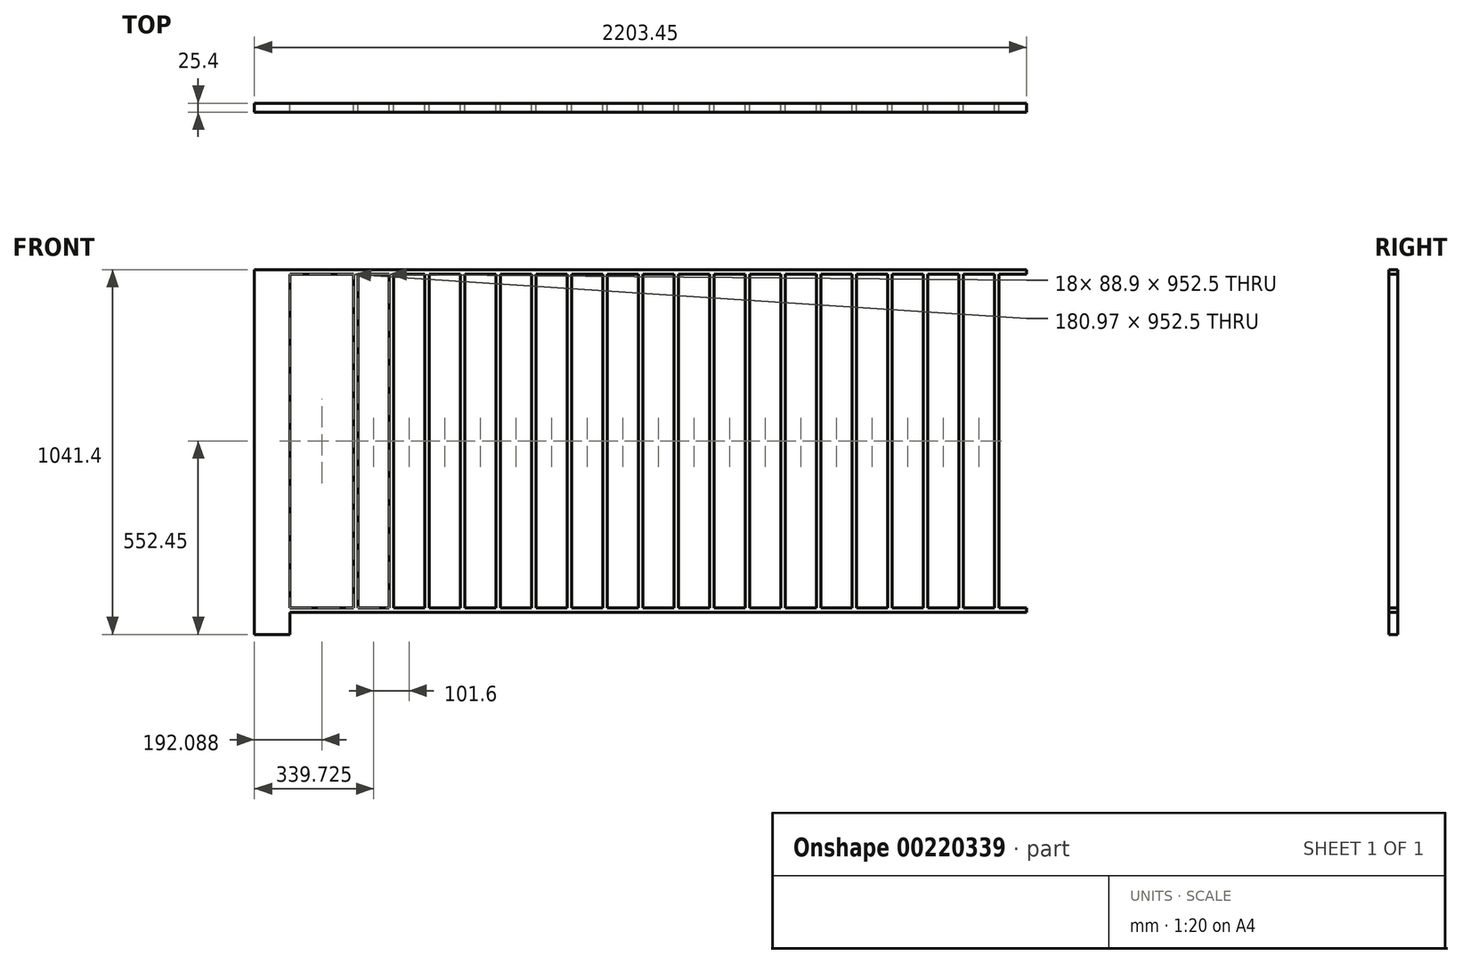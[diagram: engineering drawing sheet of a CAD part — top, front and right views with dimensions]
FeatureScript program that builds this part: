
annotation { "Feature Type Name" : "Feature", "Feature Type Description" : "" }
export const myFeature = defineFeature(function(context is Context, id is Id, definition is map)
    precondition{}
    {
        {
            var Q0;
            Q0=qCreatedBy(makeId("Front.planeOp"),FACE);
            var sketch = newSketch(context, id + "F0", { "sketchPlane" : qUnion([Q0])});
            skLineSegment(sketch, "E0.bottom", {"start": v(0, 0) * mm, "end": v(101.6, 0) * mm});
            skLineSegment(sketch, "E0.top", {"start": v(0, 1041.4) * mm, "end": v(101.6, 1041.4) * mm});
            skLineSegment(sketch, "E0.left", {"start": v(0, 0) * mm, "end": v(0, 1041.4) * mm});
            skLineSegment(sketch, "E0.right", {"start": v(101.6, 0) * mm, "end": v(101.6, 1041.4) * mm});
            skLineSegment(sketch, "E1.bottom", {"start": v(101.6, 63.5) * mm, "end": v(2203.45, 63.5) * mm});
            skLineSegment(sketch, "E1.top", {"start": v(101.6, 76.2) * mm, "end": v(2203.45, 76.2) * mm});
            skLineSegment(sketch, "E1.left", {"start": v(101.6, 63.5) * mm, "end": v(101.6, 76.2) * mm});
            skLineSegment(sketch, "E1.right", {"start": v(2203.45, 63.5) * mm, "end": v(2203.45, 76.2) * mm});
            skLineSegment(sketch, "E2.bottom", {"start": v(101.6, 1028.7) * mm, "end": v(2203.45, 1028.7) * mm});
            skLineSegment(sketch, "E2.top", {"start": v(101.6, 1041.4) * mm, "end": v(2203.45, 1041.4) * mm});
            skLineSegment(sketch, "E2.left", {"start": v(101.6, 1028.7) * mm, "end": v(101.6, 1041.4) * mm});
            skLineSegment(sketch, "E2.right", {"start": v(2203.45, 1028.7) * mm, "end": v(2203.45, 1041.4) * mm});
            skLineSegment(sketch, "E3.bottom", {"start": v(180.98, 76.2) * mm, "end": v(193.68, 76.2) * mm});
            skLineSegment(sketch, "E3.top", {"start": v(180.97, 1028.7) * mm, "end": v(193.67, 1028.7) * mm});
            skLineSegment(sketch, "E3.left", {"start": v(180.98, 76.2) * mm, "end": v(180.97, 1028.7) * mm});
            skLineSegment(sketch, "E3.right", {"start": v(193.68, 76.2) * mm, "end": v(193.67, 1028.7) * mm});
            skLineSegment(sketch, "E4.1.0.0", {"start": v(282.58, 76.2) * mm, "end": v(282.57, 1028.7) * mm});
            skLineSegment(sketch, "E4.1.0.1", {"start": v(295.28, 76.2) * mm, "end": v(295.27, 1028.7) * mm});
            skLineSegment(sketch, "E4.2.0.0", {"start": v(384.18, 76.2) * mm, "end": v(384.18, 1028.7) * mm});
            skLineSegment(sketch, "E4.2.0.1", {"start": v(396.88, 76.2) * mm, "end": v(396.88, 1028.7) * mm});
            skLineSegment(sketch, "E4.3.0.0", {"start": v(485.78, 76.2) * mm, "end": v(485.78, 1028.7) * mm});
            skLineSegment(sketch, "E4.3.0.1", {"start": v(498.48, 76.2) * mm, "end": v(498.48, 1028.7) * mm});
            skLineSegment(sketch, "E4.4.0.0", {"start": v(587.38, 76.2) * mm, "end": v(587.38, 1028.7) * mm});
            skLineSegment(sketch, "E4.4.0.1", {"start": v(600.08, 76.2) * mm, "end": v(600.08, 1028.7) * mm});
            skLineSegment(sketch, "E4.5.0.0", {"start": v(688.98, 76.2) * mm, "end": v(688.98, 1028.7) * mm});
            skLineSegment(sketch, "E4.5.0.1", {"start": v(701.68, 76.2) * mm, "end": v(701.68, 1028.7) * mm});
            skLineSegment(sketch, "E4.6.0.0", {"start": v(790.58, 76.2) * mm, "end": v(790.58, 1028.7) * mm});
            skLineSegment(sketch, "E4.6.0.1", {"start": v(803.28, 76.2) * mm, "end": v(803.28, 1028.7) * mm});
            skLineSegment(sketch, "E4.7.0.0", {"start": v(892.18, 76.2) * mm, "end": v(892.18, 1028.7) * mm});
            skLineSegment(sketch, "E4.7.0.1", {"start": v(904.88, 76.2) * mm, "end": v(904.88, 1028.7) * mm});
            skLineSegment(sketch, "E4.8.0.0", {"start": v(993.78, 76.2) * mm, "end": v(993.78, 1028.7) * mm});
            skLineSegment(sketch, "E4.8.0.1", {"start": v(1006.48, 76.2) * mm, "end": v(1006.48, 1028.7) * mm});
            skLineSegment(sketch, "E4.9.0.0", {"start": v(1095.38, 76.2) * mm, "end": v(1095.38, 1028.7) * mm});
            skLineSegment(sketch, "E4.9.0.1", {"start": v(1108.08, 76.2) * mm, "end": v(1108.08, 1028.7) * mm});
            skLineSegment(sketch, "E4.10.0.0", {"start": v(1196.98, 76.2) * mm, "end": v(1196.98, 1028.7) * mm});
            skLineSegment(sketch, "E4.10.0.1", {"start": v(1209.68, 76.2) * mm, "end": v(1209.68, 1028.7) * mm});
            skLineSegment(sketch, "E4.11.0.0", {"start": v(1298.58, 76.2) * mm, "end": v(1298.58, 1028.7) * mm});
            skLineSegment(sketch, "E4.11.0.1", {"start": v(1311.28, 76.2) * mm, "end": v(1311.28, 1028.7) * mm});
            skLineSegment(sketch, "E4.12.0.0", {"start": v(1400.18, 76.2) * mm, "end": v(1400.18, 1028.7) * mm});
            skLineSegment(sketch, "E4.12.0.1", {"start": v(1412.88, 76.2) * mm, "end": v(1412.88, 1028.7) * mm});
            skLineSegment(sketch, "E4.13.0.0", {"start": v(1501.78, 76.2) * mm, "end": v(1501.78, 1028.7) * mm});
            skLineSegment(sketch, "E4.13.0.1", {"start": v(1514.48, 76.2) * mm, "end": v(1514.48, 1028.7) * mm});
            skLineSegment(sketch, "E4.14.0.0", {"start": v(1603.38, 76.2) * mm, "end": v(1603.38, 1028.7) * mm});
            skLineSegment(sketch, "E4.14.0.1", {"start": v(1616.08, 76.2) * mm, "end": v(1616.08, 1028.7) * mm});
            skLineSegment(sketch, "E4.15.0.0", {"start": v(1704.98, 76.2) * mm, "end": v(1704.98, 1028.7) * mm});
            skLineSegment(sketch, "E4.15.0.1", {"start": v(1717.68, 76.2) * mm, "end": v(1717.68, 1028.7) * mm});
            skLineSegment(sketch, "E4.16.0.0", {"start": v(1806.58, 76.2) * mm, "end": v(1806.58, 1028.7) * mm});
            skLineSegment(sketch, "E4.16.0.1", {"start": v(1819.28, 76.2) * mm, "end": v(1819.28, 1028.7) * mm});
            skLineSegment(sketch, "E4.17.0.0", {"start": v(1908.18, 76.2) * mm, "end": v(1908.18, 1028.7) * mm});
            skLineSegment(sketch, "E4.17.0.1", {"start": v(1920.88, 76.2) * mm, "end": v(1920.88, 1028.7) * mm});
            skLineSegment(sketch, "E4.direction1", {"start": v(180.98, 76.2) * mm, "end": v(282.58, 76.2) * mm, "construction": true});
            skLineSegment(sketch, "E5.1.0.0", {"start": v(2009.78, 76.2) * mm, "end": v(2009.78, 1028.7) * mm});
            skLineSegment(sketch, "E5.1.0.1", {"start": v(2022.48, 76.2) * mm, "end": v(2022.48, 1028.7) * mm});
            skLineSegment(sketch, "E5.2.0.0", {"start": v(2111.38, 76.2) * mm, "end": v(2111.38, 1028.7) * mm});
            skLineSegment(sketch, "E5.2.0.1", {"start": v(2124.08, 76.2) * mm, "end": v(2124.08, 1028.7) * mm});
            skLineSegment(sketch, "E5.direction1", {"start": v(1908.18, 76.2) * mm, "end": v(2009.78, 76.2) * mm, "construction": true});
            skSolve(sketch);
        }
        {
            var Q0;
            {var subQ1=sQuery(id+"F0.wireOp",EDGE,"E0.bottom");Q0=makeQuery(id+"F0.imprint","IMPRINT",FACE,{"disambiguationData":[TD([[makeQuery(id+"F0.imprint","IMPRINT",EDGE,{"derivedFrom":subQ1}),1.0]])]});}
            var Q1;
            {var subQ24=sQuery(id+"F0.wireOp",EDGE,"E1.bottom");Q1=makeQuery(id+"F0.imprint","IMPRINT",FACE,{"disambiguationData":[TD([[makeQuery(id+"F0.imprint","IMPRINT",EDGE,{"derivedFrom":subQ24}),1.0]])]});}
            var Q2;
            Q2=makeQuery(id+"F0.imprint","IMPRINT",FACE,{"disambiguationData":[TD([[makeQuery(id+"F0.imprint","IMPRINT",EDGE,{"derivedFrom":sQuery(id+"F0.wireOp",EDGE,"E3.bottom")}),1.0]])]});
            var Q3;
            {var subQ0=sQuery(id+"F0.wireOp",EDGE,"E4.1.0.0");Q3=makeQuery(id+"F0.imprint","IMPRINT",FACE,{"disambiguationData":[TD([[makeQuery(id+"F0.imprint","IMPRINT",EDGE,{"derivedFrom":subQ0}),-1.0]])]});}
            var Q4;
            {var subQ0=sQuery(id+"F0.wireOp",EDGE,"E4.2.0.0");Q4=makeQuery(id+"F0.imprint","IMPRINT",FACE,{"disambiguationData":[TD([[makeQuery(id+"F0.imprint","IMPRINT",EDGE,{"derivedFrom":subQ0}),-1.0]])]});}
            var Q5;
            {var subQ0=sQuery(id+"F0.wireOp",EDGE,"E4.3.0.0");Q5=makeQuery(id+"F0.imprint","IMPRINT",FACE,{"disambiguationData":[TD([[makeQuery(id+"F0.imprint","IMPRINT",EDGE,{"derivedFrom":subQ0}),-1.0]])]});}
            var Q6;
            {var subQ0=sQuery(id+"F0.wireOp",EDGE,"E4.4.0.0");Q6=makeQuery(id+"F0.imprint","IMPRINT",FACE,{"disambiguationData":[TD([[makeQuery(id+"F0.imprint","IMPRINT",EDGE,{"derivedFrom":subQ0}),-1.0]])]});}
            var Q7;
            {var subQ0=sQuery(id+"F0.wireOp",EDGE,"E4.5.0.0");Q7=makeQuery(id+"F0.imprint","IMPRINT",FACE,{"disambiguationData":[TD([[makeQuery(id+"F0.imprint","IMPRINT",EDGE,{"derivedFrom":subQ0}),-1.0]])]});}
            var Q8;
            {var subQ0=sQuery(id+"F0.wireOp",EDGE,"E4.6.0.0");Q8=makeQuery(id+"F0.imprint","IMPRINT",FACE,{"disambiguationData":[TD([[makeQuery(id+"F0.imprint","IMPRINT",EDGE,{"derivedFrom":subQ0}),-1.0]])]});}
            var Q9;
            {var subQ0=sQuery(id+"F0.wireOp",EDGE,"E4.7.0.0");Q9=makeQuery(id+"F0.imprint","IMPRINT",FACE,{"disambiguationData":[TD([[makeQuery(id+"F0.imprint","IMPRINT",EDGE,{"derivedFrom":subQ0}),-1.0]])]});}
            var Q10;
            {var subQ0=sQuery(id+"F0.wireOp",EDGE,"E4.8.0.0");Q10=makeQuery(id+"F0.imprint","IMPRINT",FACE,{"disambiguationData":[TD([[makeQuery(id+"F0.imprint","IMPRINT",EDGE,{"derivedFrom":subQ0}),-1.0]])]});}
            var Q11;
            {var subQ0=sQuery(id+"F0.wireOp",EDGE,"E4.9.0.0");Q11=makeQuery(id+"F0.imprint","IMPRINT",FACE,{"disambiguationData":[TD([[makeQuery(id+"F0.imprint","IMPRINT",EDGE,{"derivedFrom":subQ0}),-1.0]])]});}
            var Q12;
            {var subQ0=sQuery(id+"F0.wireOp",EDGE,"E4.10.0.0");Q12=makeQuery(id+"F0.imprint","IMPRINT",FACE,{"disambiguationData":[TD([[makeQuery(id+"F0.imprint","IMPRINT",EDGE,{"derivedFrom":subQ0}),-1.0]])]});}
            var Q13;
            {var subQ0=sQuery(id+"F0.wireOp",EDGE,"E4.11.0.0");Q13=makeQuery(id+"F0.imprint","IMPRINT",FACE,{"disambiguationData":[TD([[makeQuery(id+"F0.imprint","IMPRINT",EDGE,{"derivedFrom":subQ0}),-1.0]])]});}
            var Q14;
            {var subQ0=sQuery(id+"F0.wireOp",EDGE,"E4.12.0.0");Q14=makeQuery(id+"F0.imprint","IMPRINT",FACE,{"disambiguationData":[TD([[makeQuery(id+"F0.imprint","IMPRINT",EDGE,{"derivedFrom":subQ0}),-1.0]])]});}
            var Q15;
            {var subQ0=sQuery(id+"F0.wireOp",EDGE,"E4.13.0.0");Q15=makeQuery(id+"F0.imprint","IMPRINT",FACE,{"disambiguationData":[TD([[makeQuery(id+"F0.imprint","IMPRINT",EDGE,{"derivedFrom":subQ0}),-1.0]])]});}
            var Q16;
            {var subQ0=sQuery(id+"F0.wireOp",EDGE,"E4.14.0.0");Q16=makeQuery(id+"F0.imprint","IMPRINT",FACE,{"disambiguationData":[TD([[makeQuery(id+"F0.imprint","IMPRINT",EDGE,{"derivedFrom":subQ0}),-1.0]])]});}
            var Q17;
            {var subQ0=sQuery(id+"F0.wireOp",EDGE,"E4.15.0.0");Q17=makeQuery(id+"F0.imprint","IMPRINT",FACE,{"disambiguationData":[TD([[makeQuery(id+"F0.imprint","IMPRINT",EDGE,{"derivedFrom":subQ0}),-1.0]])]});}
            var Q18;
            {var subQ0=sQuery(id+"F0.wireOp",EDGE,"E4.16.0.0");Q18=makeQuery(id+"F0.imprint","IMPRINT",FACE,{"disambiguationData":[TD([[makeQuery(id+"F0.imprint","IMPRINT",EDGE,{"derivedFrom":subQ0}),-1.0]])]});}
            var Q19;
            {var subQ0=sQuery(id+"F0.wireOp",EDGE,"E4.17.0.0");Q19=makeQuery(id+"F0.imprint","IMPRINT",FACE,{"disambiguationData":[TD([[makeQuery(id+"F0.imprint","IMPRINT",EDGE,{"derivedFrom":subQ0}),-1.0]])]});}
            var Q20;
            {var subQ3=sQuery(id+"F0.wireOp",EDGE,"c8Zv6VXj-JrFF-Rrpw-kdWE-uJ8zpSaiPQ5N.bottom");Q20=makeQuery(id+"F0.imprint","IMPRINT",FACE,{"disambiguationData":[TD([[makeQuery(id+"F0.imprint","IMPRINT",EDGE,{"derivedFrom":subQ3}),-1.0]])]});}
            var Q21;
            {var subQ16=sQuery(id+"F0.wireOp",EDGE,"E2.top");Q21=makeQuery(id+"F0.imprint","IMPRINT",FACE,{"disambiguationData":[TD([[makeQuery(id+"F0.imprint","IMPRINT",EDGE,{"derivedFrom":subQ16}),-1.0]])]});}
            var Q22;
            {var subQ0=sQuery(id+"F0.wireOp",EDGE,"E5.1.0.0");Q22=makeQuery(id+"F0.imprint","IMPRINT",FACE,{"disambiguationData":[TD([[makeQuery(id+"F0.imprint","IMPRINT",EDGE,{"derivedFrom":subQ0}),-1.0]])]});}
            var Q23;
            {var subQ0=sQuery(id+"F0.wireOp",EDGE,"E5.2.0.0");Q23=makeQuery(id+"F0.imprint","IMPRINT",FACE,{"disambiguationData":[TD([[makeQuery(id+"F0.imprint","IMPRINT",EDGE,{"derivedFrom":subQ0}),-1.0]])]});}
            extrude(context, id + "F1", {"entities" : qUnion([Q0, Q1, Q2, Q3, Q4, Q5, Q6, Q7, Q8, Q9, Q10, Q11, Q12, Q13, Q14, Q15, Q16, Q17, Q18, Q19, Q20, Q21, Q22, Q23]), "depth" : 25.4 * mm});
        }
    });
